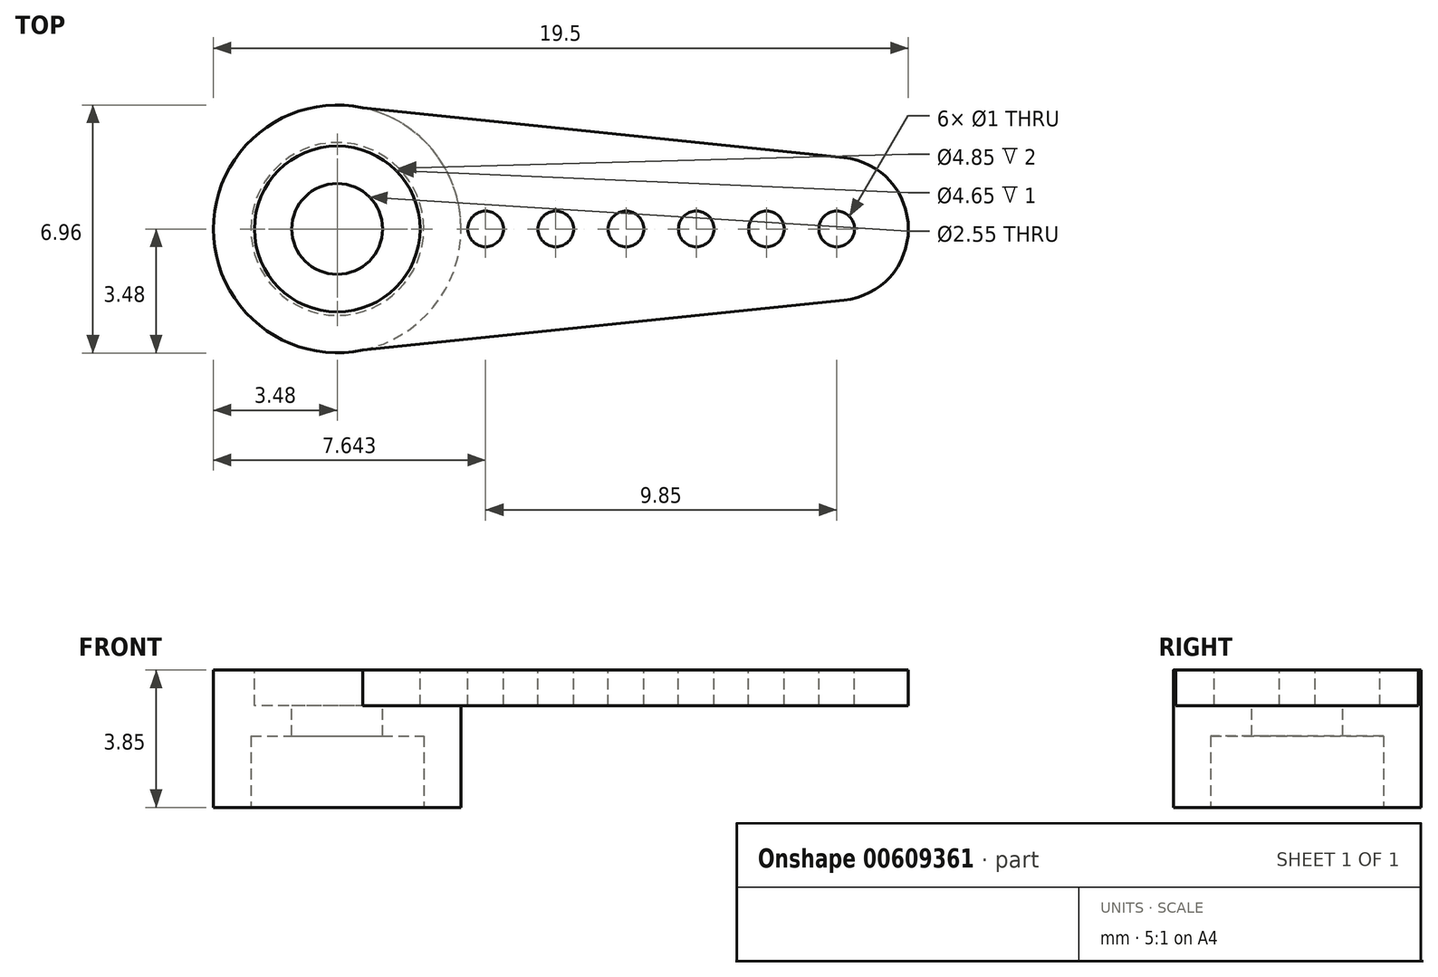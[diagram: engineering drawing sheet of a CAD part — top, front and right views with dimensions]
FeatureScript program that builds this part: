
annotation { "Feature Type Name" : "Feature", "Feature Type Description" : "" }
export const myFeature = defineFeature(function(context is Context, id is Id, definition is map)
    precondition{}
    {
        {
            var Q0;
            Q0=qCreatedBy(makeId("Top.planeOp"),FACE);
            var sketch = newSketch(context, id + "F0", { "sketchPlane" : qUnion([Q0])});
            skCircle(sketch, "E0", {"center": v(0, 0) * mm, "radius": 3.48 * mm});
            skSolve(sketch);
        }
        {
            var Q0;
            Q0=makeQuery(id+"F0.imprint","IMPRINT",FACE,{"disambiguationData":[TD([[makeQuery(id+"F0.imprint","IMPRINT",EDGE,{"derivedFrom":sQuery(id+"F0.wireOp",EDGE,"E0")}),1.0]])]});
            extrude(context, id + "F1", {"entities" : qUnion([Q0]), "depth" : 3.85 * mm, "offsetDistance" : 25 * mm});
        }
        {
            var Q0;
            Q0=makeQuery(id+"F1.opExtrude","CAP_FACE",FACE,{"disambiguationData":[OSD([sQuery(id+"F0.wireOp",EDGE,"E0")])],"isStart":true});
            var sketch = newSketch(context, id + "F2", { "sketchPlane" : qUnion([Q0])});
            skCircle(sketch, "E1", {"center": v(0, 0) * mm, "radius": 2.43 * mm});
            skSolve(sketch);
        }
        {
            var Q0;
            Q0=qSketchRegion(id+"F2",true);
            extrude(context, id + "F3", {"entities" : qUnion([Q0]), "operationType" : NewBodyOperationType.REMOVE, "oppositeDirection" : true, "depth" : 2 * mm, "offsetDistance" : 25 * mm});
        }
        {
            var Q0;
            Q0=makeQuery(id+"F1.opExtrude","CAP_FACE",FACE,{"disambiguationData":[OSD([sQuery(id+"F0.wireOp",EDGE,"E0")])],"isStart":false});
            var sketch = newSketch(context, id + "F4", { "sketchPlane" : qUnion([Q0])});
            skArc(sketch, "E2.0", {"start": v(0, 3.48) * mm, "mid": v(-3.48, 0) * mm, "end": v(0, -3.48) * mm});
            skLineSegment(sketch, "E3", {"start": v(0, 3.47) * mm, "end": v(14.22, 2) * mm});
            skLineSegment(sketch, "E4", {"start": v(0, -3.48) * mm, "end": v(14.22, -2) * mm});
            skLineSegment(sketch, "E5", {"start": v(0, 0) * mm, "end": v(14.22, 0) * mm, "construction": true});
            skLineSegment(sketch, "E6", {"start": v(14.22, 2) * mm, "end": v(14.22, 0) * mm, "construction": true});
            skLineSegment(sketch, "E7", {"start": v(14.22, 0) * mm, "end": v(14.22, -2) * mm, "construction": true});
            skArc(sketch, "E8", {"start": v(14.22, 2) * mm, "mid": v(16.02, 0) * mm, "end": v(14.22, -2) * mm});
            skSolve(sketch);
        }
        {
            var Q0;
            Q0=qSketchRegion(id+"F4",true);
            extrude(context, id + "F5", {"entities" : qUnion([Q0]), "operationType" : NewBodyOperationType.ADD, "oppositeDirection" : true, "depth" : 1 * mm, "offsetDistance" : 25 * mm});
        }
        {
            var Q0;
            Q0=makeQuery(id+"F5.boolean.opBoolean","MERGE",FACE,{"derivedFrom":[makeQuery(id+"F1.opExtrude","CAP_FACE",FACE,{"disambiguationData":[OSD([sQuery(id+"F0.wireOp",EDGE,"E0")])],"isStart":false}),makeQuery(id+"F5.opExtrude","CAP_FACE",FACE,{"disambiguationData":[OSD([sQuery(id+"F4.wireOp",EDGE,"E2.0"),sQuery(id+"F4.wireOp",EDGE,"E3"),sQuery(id+"F4.wireOp",EDGE,"E4"),sQuery(id+"F4.wireOp",EDGE,"E8")])],"isStart":true})]});
            var sketch = newSketch(context, id + "F6", { "sketchPlane" : qUnion([Q0])});
            skCircle(sketch, "E9", {"center": v(0, 0) * mm, "radius": 2.33 * mm});
            skSolve(sketch);
        }
        {
            var Q0;
            Q0=qSketchRegion(id+"F6",true);
            extrude(context, id + "F7", {"entities" : qUnion([Q0]), "operationType" : NewBodyOperationType.REMOVE, "oppositeDirection" : true, "depth" : 1 * mm, "offsetDistance" : 25 * mm});
        }
        {
            var Q0;
            Q0=makeQuery(id+"F7.boolean.opBoolean","COPY",FACE,{"derivedFrom":makeQuery(id+"F7.opExtrude","CAP_FACE",FACE,{"disambiguationData":[OSD([sQuery(id+"F6.wireOp",EDGE,"E9")])],"isStart":false})});
            var sketch = newSketch(context, id + "F8", { "sketchPlane" : qUnion([Q0])});
            skCircle(sketch, "E10", {"center": v(0, 0) * mm, "radius": 1.27 * mm});
            skSolve(sketch);
        }
        {
            var Q0;
            Q0=qSketchRegion(id+"F8",true);
            extrude(context, id + "F9", {"entities" : qUnion([Q0]), "operationType" : NewBodyOperationType.REMOVE, "endBound" : BoundingType.THROUGH_ALL, "oppositeDirection" : true, "depth" : 25 * mm, "offsetDistance" : 25 * mm});
        }
        {
            var Q0;
            Q0=makeQuery(id+"F5.boolean.opBoolean","MERGE",FACE,{"derivedFrom":[makeQuery(id+"F1.opExtrude","CAP_FACE",FACE,{"disambiguationData":[OSD([sQuery(id+"F0.wireOp",EDGE,"E0")])],"isStart":false}),makeQuery(id+"F5.opExtrude","CAP_FACE",FACE,{"disambiguationData":[OSD([sQuery(id+"F4.wireOp",EDGE,"E2.0"),sQuery(id+"F4.wireOp",EDGE,"E3"),sQuery(id+"F4.wireOp",EDGE,"E4"),sQuery(id+"F4.wireOp",EDGE,"E8")])],"isStart":true})]});
            var sketch = newSketch(context, id + "F10", { "sketchPlane" : qUnion([Q0])});
            skCircle(sketch, "E11", {"center": v(14.01, 0) * mm, "radius": 0.5 * mm});
            skCircle(sketch, "E12.1.0.0", {"center": v(12.04, 0) * mm, "radius": 0.5 * mm});
            skCircle(sketch, "E12.2.0.0", {"center": v(10.07, 0) * mm, "radius": 0.5 * mm});
            skCircle(sketch, "E12.3.0.0", {"center": v(8.1, 0) * mm, "radius": 0.5 * mm});
            skCircle(sketch, "E12.4.0.0", {"center": v(6.13, 0) * mm, "radius": 0.5 * mm});
            skCircle(sketch, "E12.5.0.0", {"center": v(4.16, 0) * mm, "radius": 0.5 * mm});
            skLineSegment(sketch, "E12.direction1", {"start": v(14.01, 0) * mm, "end": v(12.04, 0) * mm, "construction": true});
            skSolve(sketch);
        }
        {
            var Q0;
            Q0=qSketchRegion(id+"F10",true);
            extrude(context, id + "F11", {"entities" : qUnion([Q0]), "operationType" : NewBodyOperationType.REMOVE, "endBound" : BoundingType.THROUGH_ALL, "oppositeDirection" : true, "depth" : 25 * mm, "offsetDistance" : 25 * mm});
        }
    });
